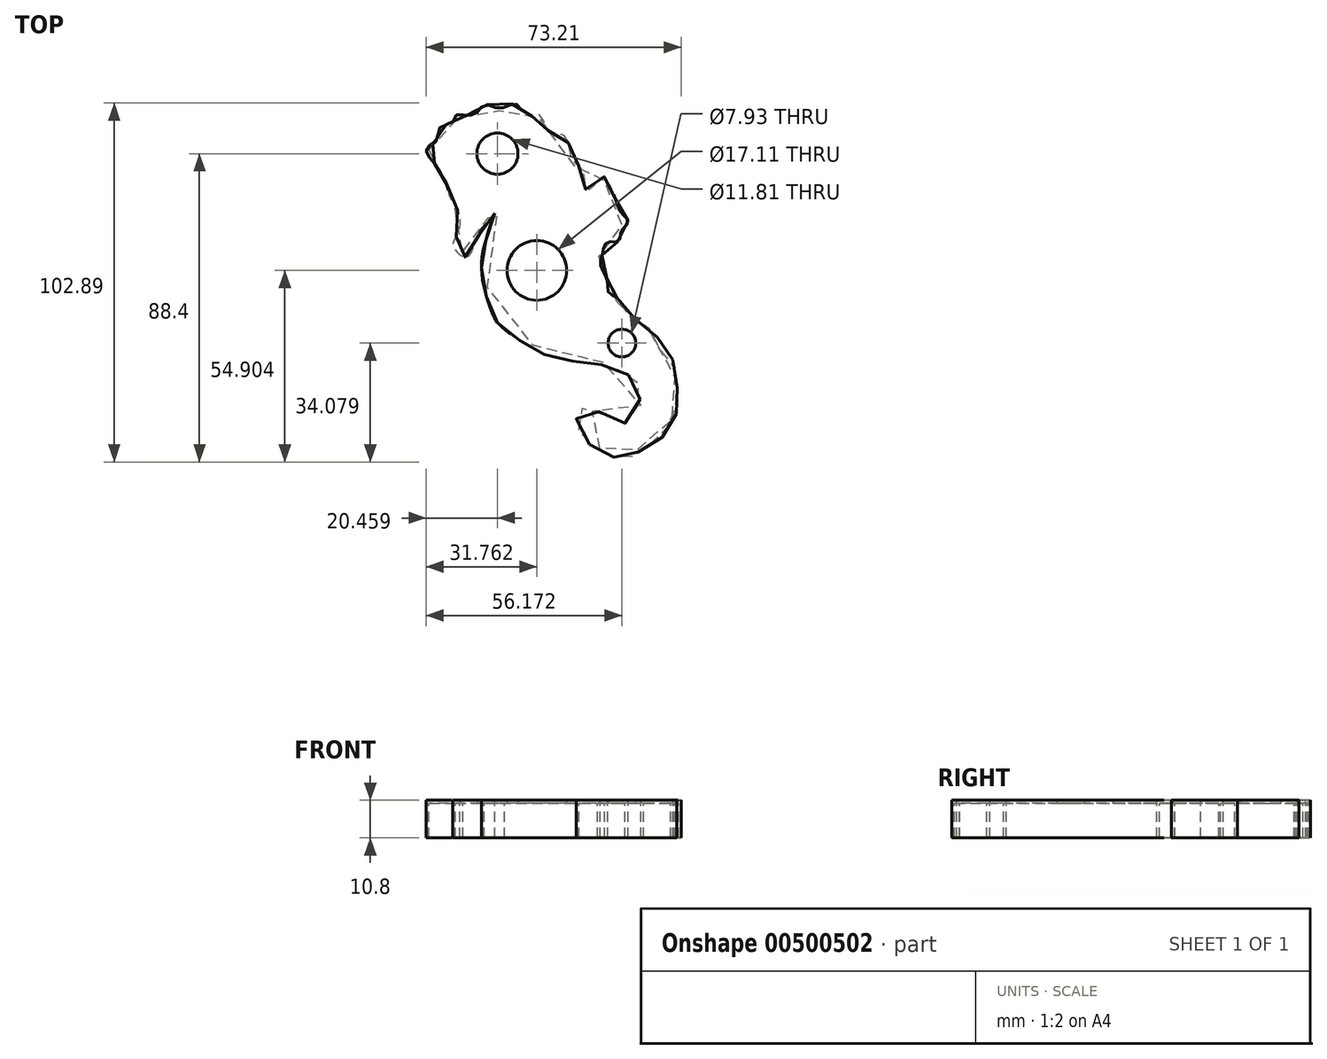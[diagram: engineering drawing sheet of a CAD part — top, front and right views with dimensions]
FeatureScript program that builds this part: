
annotation { "Feature Type Name" : "Feature", "Feature Type Description" : "" }
export const myFeature = defineFeature(function(context is Context, id is Id, definition is map)
    precondition{}
    {
        {
            var Q0;
            Q0=qCreatedBy(makeId("Top.planeOp"),FACE);
            var sketch = newSketch(context, id + "F0", { "sketchPlane" : qUnion([Q0])});
            skFitSpline(sketch, "E0", {"points": [v(-35.2, 25.55) * mm, v(-31.76, 20.6) * mm, v(-30.86, 18.59) * mm, v(-29.14, 15.56) * mm, v(-28.44, 12.24) * mm, v(-25.71, 7.3) * mm, v(-26.72, 0) * mm, v(-27.53, -1.78) * mm, v(-24.6, -4.4) * mm, v(-23, -1.38) * mm, v(-21.48, 1.65) * mm, v(-20.77, 3.26) * mm, v(-18.35, 5.78) * mm, v(-15.43, 10.72) * mm, v(-14.32, 12.44) * mm, v(-13.61, 12.54) * mm, v(-14.92, 8.4) * mm, v(-16.23, 5.48) * mm, v(-17.95, 0) * mm, v(-19.36, -8.24) * mm, v(-17.44, -17.72) * mm, v(-14.62, -23.77) * mm, v(-7.86, -28.91) * mm, v(0, -33.05) * mm, v(8.17, -34.46) * mm, v(13.72, -35.06) * mm, v(21.18, -37.58) * mm, v(25.52, -40.91) * mm, v(26.33, -44.95) * mm, v(22.4, -53.01) * mm, v(18.36, -53.52) * mm, v(14.53, -51.1) * mm, v(10.7, -49.18) * mm, v(8.78, -49.48) * mm, v(7.87, -52) * mm, v(10.3, -57.35) * mm, v(14.22, -60.38) * mm, v(15.13, -61.69) * mm, v(18.06, -61.79) * mm, v(21.48, -63.1) * mm, v(23.8, -60.68) * mm, v(26.43, -59.87) * mm, v(28.95, -57.15) * mm, v(31.67, -55.84) * mm, v(32.78, -53.01) * mm, v(35, -51.2) * mm, v(34.8, -47.97) * mm, v(36.41, -45.15) * mm, v(35.2, -42.73) * mm, v(35.5, -39.8) * mm, v(34.2, -37.58) * mm, v(33.79, -34.56) * mm, v(30.26, -31.84) * mm, v(29.25, -27.9) * mm, v(24.5, -24.57) * mm, v(22.8, -23.06) * mm, v(20.98, -22.56) * mm, v(19.16, -19.63) * mm, v(18.36, -17.62) * mm, v(15.53, -15.6) * mm, v(15.13, -11.87) * mm, v(13.21, -7.83) * mm, v(13.82, -4) * mm, v(14.32, -1.68) * mm, v(16.24, 0) * mm, v(18.66, 0) * mm, v(19.06, 2.35) * mm, v(21.08, 4.98) * mm, v(19.27, 7) * mm, v(17.25, 12.14) * mm, v(16.54, 13.75) * mm, v(14.63, 17.18) * mm, v(12.5, 14.56) * mm, v(9.28, 13.45) * mm, v(8.37, 19) * mm, v(5.25, 22.32) * mm, v(3.23, 28.88) * mm, v(-1.3, 30.29) * mm, v(-3.63, 34.83) * mm, v(-4.23, 34.42) * mm, v(-8.17, 35.53) * mm, v(-10.89, 38.15) * mm, v(-11.9, 37.45) * mm, v(-16.23, 36.84) * mm, v(-19.06, 37.65) * mm, v(-20.77, 35.73) * mm, v(-25, 34.63) * mm, v(-26.72, 35.03) * mm, v(-27.73, 33.01) * mm, v(-31.36, 31.5) * mm, v(-31.76, 29.68) * mm, v(-33.28, 26.76) * mm, v(-35.2, 25.55) * mm]});
            skSolve(sketch);
        }
        {
            var Q0;
            Q0=makeQuery(id+"F0.imprint","IMPRINT",FACE,{"disambiguationData":[TD([[makeQuery(id+"F0.imprint","IMPRINT",EDGE,{"derivedFrom":sQuery(id+"F0.wireOp",EDGE,"E0")}),1.0]])]});
            var Q1;
            Q1=sQuery(id+"F0.wireOp",EDGE,"E0");
            extrude(context, id + "F1", {"entities" : qUnion([Q0]), "surfaceEntities" : qUnion([Q1]), "oppositeDirection" : true, "depth" : 10 * mm});
        }
        {
            var Q0;
            Q0=makeQuery(id+"F1.opExtrude","CAP_FACE",FACE,{"disambiguationData":[OSD([sQuery(id+"F0.wireOp",EDGE,"E0")])],"isStart":false});
            shell(context, id + "F2", {"entities" : qUnion([Q0]), "thickness" : .8 * mm, "oppositeDirection" : true});
        }
        {
            var Q0;
            Q0=makeQuery(id+"F0.imprint","IMPRINT",FACE,{"disambiguationData":[TD([[makeQuery(id+"F0.imprint","IMPRINT",EDGE,{"derivedFrom":sQuery(id+"F0.wireOp",EDGE,"E0")}),1.0]])]});
            var sketch = newSketch(context, id + "F3", { "sketchPlane" : qUnion([Q0])});
            skCircle(sketch, "E1", {"center": v(-15.54, 24.47) * mm, "radius": 5.9 * mm});
            skCircle(sketch, "E2", {"center": v(-4.24, -9.03) * mm, "radius": 8.55 * mm});
            skCircle(sketch, "E3", {"center": v(20.17, -29.85) * mm, "radius": 3.97 * mm});
            skSolve(sketch);
        }
        {
            var Q0;
            Q0 = qSketchRegion(id + "F3", true);
            extrude(context, id + "F4", {"entities" : qUnion([Q0]), "operationType" : NewBodyOperationType.REMOVE, "depth" : 8.7 * mm});
        }
    });
